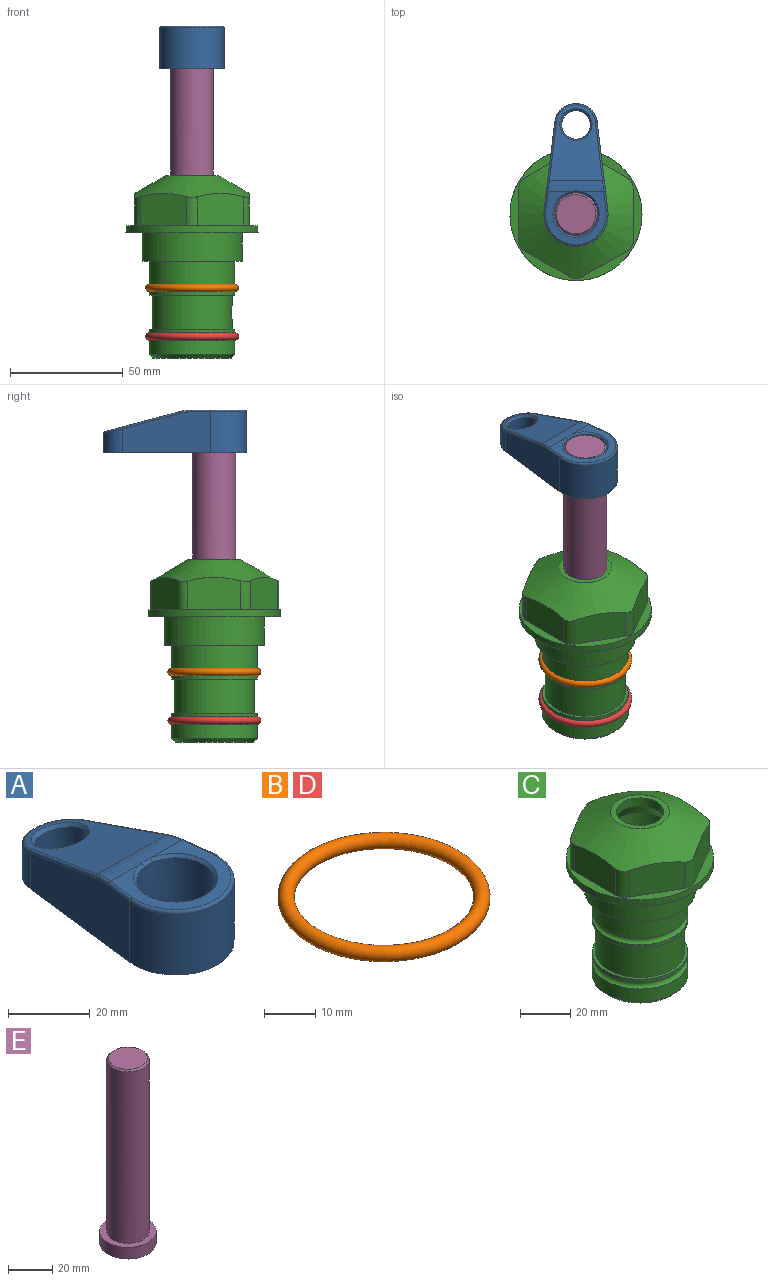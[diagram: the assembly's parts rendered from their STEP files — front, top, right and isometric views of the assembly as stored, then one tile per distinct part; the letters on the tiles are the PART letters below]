
ASSEMBLY  parts=5 mates=4
PART A: 31 faces, bbox 31.7x65.5x19.8 mm
  f0: plane 39.12x18.26mm, normal (0.99,0.12,0), area 612.2mm2, adj f1,f4,f7,f11,f13,f15
  f1: cylinder r=9.53mm len=18.91mm, axis (0,0,-1), area 296.1mm2, adj f0,f2,f7,f17
  f2: plane 39.12x18.26mm, normal (-0.99,0.12,0), area 612.2mm2, adj f1,f4,f7,f12,f14,f16
  f3: cylinder r=6.35mm len=12.7mm, axis (0,0,-1), area 362.4mm2, adj f7,f18
  f4: cylinder r=14.29mm len=28.58mm, axis (0,0,-1), area 882.2mm2, adj f0,f2,f7,f10
  f5: cylinder r=9.53mm len=19.05mm, axis (0,0,-1), area 1092.6mm2, adj f7,f19,f20
  f6: plane 26.99x23.69mm, normal (0,0,1), area 216.2mm2, adj f9,f10,f11,f12,f19
  f7: plane 63.5x28.58mm, normal (0,0,-1), area 661.8mm2, adj f0,f1,f2,f3,f4,f5,f22,f23
  f8: plane 33.52x23.6mm, normal (0,0.26,0.97), area 486mm2, adj f9,f15,f16,f17,f18
  f9: cylinder r=19.05mm len=24.72mm, axis (1,0,0), area 120.4mm2, adj f6,f8,f13,f14,f20
  f10: torus R=13.49mm, axis (0,0,1), area 59mm2, adj f4,f6,f11,f12
  f11: cylinder r=0.79mm len=8.67mm, axis (0.12,-0.99,0), area 10.8mm2, adj f0,f6,f10,f13
  f12: cylinder r=0.79mm len=8.67mm, axis (0.12,0.99,0), area 10.8mm2, adj f2,f6,f10,f14
  f13: bspline ~4.95x1.42mm, area 6.1mm2, adj f0,f9,f11,f15
  f14: bspline ~4.95x1.42mm, area 6.1mm2, adj f2,f9,f12,f16
  f15: cylinder r=0.79mm len=25.95mm, axis (0.12,-0.96,0.26), area 32.9mm2, adj f0,f8,f13,f17
  f16: cylinder r=0.79mm len=25.95mm, axis (0.12,0.96,-0.26), area 32.9mm2, adj f2,f8,f14,f17
  f17: bspline ~18.91x8.38mm, area 30mm2, adj f1,f8,f15,f16
  f18: bspline ~14.29x14.29mm, area 48.3mm2, adj f3,f8
  f19: cone r=9.53mm half-angle=45deg, axis (0,0,1), area 66.5mm2, adj f5,f6,f20
  f20: bspline ~3.22x0.96mm, area 3.5mm2, adj f5,f9,f19
  f21: plane 2.75x2.72mm, normal (0,0,-1), area 2.9mm2, adj f23,f25,f28
  f22: plane 23.05x15.88mm, normal (-0.99,-0.12,0), area 323.6mm2, adj f7,f25,f26,f27,f28,f29
  f23: plane 23.05x15.88mm, normal (0.99,-0.12,0), area 323.6mm2, adj f7,f21,f25,f27,f28,f30
  f24: cylinder r=9.53mm len=10.69mm, axis (0,0,-1), area 114.7mm2, adj f7,f27,f29,f30
  f25: cylinder r=12.7mm len=20.59mm, axis (0,0,-1), area 381.1mm2, adj f7,f21,f22,f23,f26,f28
  f26: plane 2.75x2.72mm, normal (0,0,-1), area 2.9mm2, adj f22,f25,f28
  f27: plane 19.72x18.37mm, normal (0,-0.26,-0.97), area 291.8mm2, adj f22,f23,f24,f28,f29,f30
  f28: cylinder r=15.88mm len=19.92mm, axis (1,0,0), area 54.8mm2, adj f21,f22,f23,f25,f26,f27
  f29: cylinder r=1.59mm len=11mm, axis (0,0,-1), area 34.7mm2, adj f7,f22,f24,f27
  f30: cylinder r=1.59mm len=11mm, axis (0,0,-1), area 34.7mm2, adj f7,f23,f24,f27
PART B: 1 faces, bbox 44.7x44.7x3.2 mm
  f0: torus R=19.05mm, axis (0,0,1), area 1193.9mm2
PART C: 36 faces, bbox 58.7x58.7x81 mm
  f0: cylinder r=17.78mm len=35.56mm, axis (0,0,1), area 1670.8mm2, adj f23,f24,f31
  f1: cylinder r=19.05mm len=38.1mm, axis (0,0,1), area 1191.9mm2, adj f26,f27,f30
  f2: plane 58.66x58.66mm, normal (0,0,-1), area 1150.6mm2, adj f3,f28
  f3: cylinder r=29.33mm len=58.66mm, axis (0,0,-1), area 585.1mm2, adj f2,f4
  f4: plane 58.66x58.66mm, normal (0,0,1), area 475.9mm2, adj f3,f5,f6,f7,f8,f9,f10,f11
  f5: plane 20.32x14.34mm, normal (-0.5,0.87,0), area 324.4mm2, adj f4,f15,f16,f17
  f6: plane 20.32x14.34mm, normal (0.5,0.87,0), area 324.4mm2, adj f4,f14,f15,f17
  f7: plane 23.48x14.34mm, normal (1,0,0), area 324.4mm2, adj f4,f13,f14,f17
  f8: plane 20.32x14.34mm, normal (0.5,-0.87,0), area 324.4mm2, adj f4,f12,f13,f17
  f9: plane 20.32x14.34mm, normal (-0.5,-0.87,0), area 324.4mm2, adj f4,f11,f12,f17
  f10: plane 23.48x14.34mm, normal (-1,0,0), area 324.4mm2, adj f4,f11,f16,f17
  f11: cylinder r=5.08mm len=12.85mm, axis (0,0,-1), area 67.2mm2, adj f4,f9,f10,f17
  f12: cylinder r=5.08mm len=12.85mm, axis (0,0,-1), area 67.2mm2, adj f4,f8,f9,f17
  f13: cylinder r=5.08mm len=12.85mm, axis (0,0,-1), area 67.2mm2, adj f4,f7,f8,f17
  f14: cylinder r=5.08mm len=12.85mm, axis (0,0,-1), area 67.2mm2, adj f4,f6,f7,f17
  f15: cylinder r=5.08mm len=12.85mm, axis (0,0,-1), area 67.2mm2, adj f4,f5,f6,f17
  f16: cylinder r=5.08mm len=12.85mm, axis (0,0,-1), area 67.2mm2, adj f4,f5,f10,f17
  f17: cone r=11.73mm half-angle=60deg, axis (0,0,-1), area 2071.8mm2, adj f5,f6,f7,f8,f9,f10,f11,f12
  f18: plane 23.46x23.46mm, normal (0,0,1), area 147.4mm2, adj f17,f35
  f19: plane 34.93x34.93mm, normal (0,0,-1), area 958mm2, adj f29
  f20: cylinder r=19.05mm len=38.1mm, axis (0,0,1), area 760.1mm2, adj f21,f29
  f21: torus R=19.05mm, axis (0,0,1), area 565.3mm2, adj f20,f22
  f22: cylinder r=19.05mm len=38.1mm, axis (0,0,1), area 190mm2, adj f21,f23
  f23: plane 38.1x38.1mm, normal (0,0,1), area 146.9mm2, adj f0,f22
  f24: plane 38.1x38.1mm, normal (0,0,-1), area 146.9mm2, adj f0,f25
  f25: cylinder r=19.05mm len=38.1mm, axis (0,0,1), area 190mm2, adj f24,f26
  f26: torus R=19.05mm, axis (0,0,1), area 565.3mm2, adj f1,f25
  f27: plane 44.45x44.45mm, normal (0,0,-1), area 411.7mm2, adj f1,f28
  f28: cylinder r=22.23mm len=44.45mm, axis (0,0,1), area 1773.5mm2, adj f2,f27
  f29: cone r=19.05mm half-angle=45deg, axis (0,0,1), area 257.5mm2, adj f19,f20
  f30: cylinder r=3.17mm len=6.75mm, axis (-1,0,0), area 128mm2, adj f1,f33
  f31: cylinder r=3.17mm len=6.35mm, axis (-1,0,0), area 102.5mm2, adj f0,f33
  f32: plane 25.4x25.4mm, normal (0,0,1), area 506.7mm2, adj f33
  f33: cylinder r=12.7mm len=66.42mm, axis (0,0,-1), area 5236.2mm2, adj f30,f31,f32,f34
  f34: cone r=9.53mm half-angle=30deg, axis (0,0,-1), area 443.4mm2, adj f33,f35
  f35: cylinder r=9.53mm len=19.05mm, axis (0,0,-1), area 240.9mm2, adj f18,f34
PART D: same geometry as B
PART E: 6 faces, bbox 25.4x25.4x101.6 mm
  f0: plane 17.46x17.46mm, normal (0,0,1), area 239.5mm2, adj f5
  f1: plane 25.4x25.4mm, normal (0,0,-1), area 506.7mm2, adj f2
  f2: cylinder r=12.7mm len=25.4mm, axis (0,0,1), area 506.7mm2, adj f1,f3
  f3: plane 25.4x25.4mm, normal (0,0,1), area 221.7mm2, adj f2,f4
  f4: cylinder r=9.53mm len=94.46mm, axis (0,0,1), area 5653mm2, adj f3,f5
  f5: cone r=8.73mm half-angle=45deg, axis (0,0,-1), area 64.4mm2, adj f0,f4
PLACE A t=(0,0,28.35)mm
PLACE B at identity
PLACE C at identity fixed
PLACE D t=(0,0,-21.59)mm
PLACE E t=(0,0,27.55)mm
MATE fastened D.f0 <-> C.f0  axis (0,0,1) through (0,0,-46.1)mm
MATE fastened B.f0 <-> C.f0  axis (0,0,1) through (0,0,-24.51)mm
MATE cylindrical C.f0 <-> E.f2  axis (0,0,1) through (0,0,-50.55)mm
MATE fastened A.f4 <-> E.f2  axis (0,0,-1) through (0,0,91.05)mm
